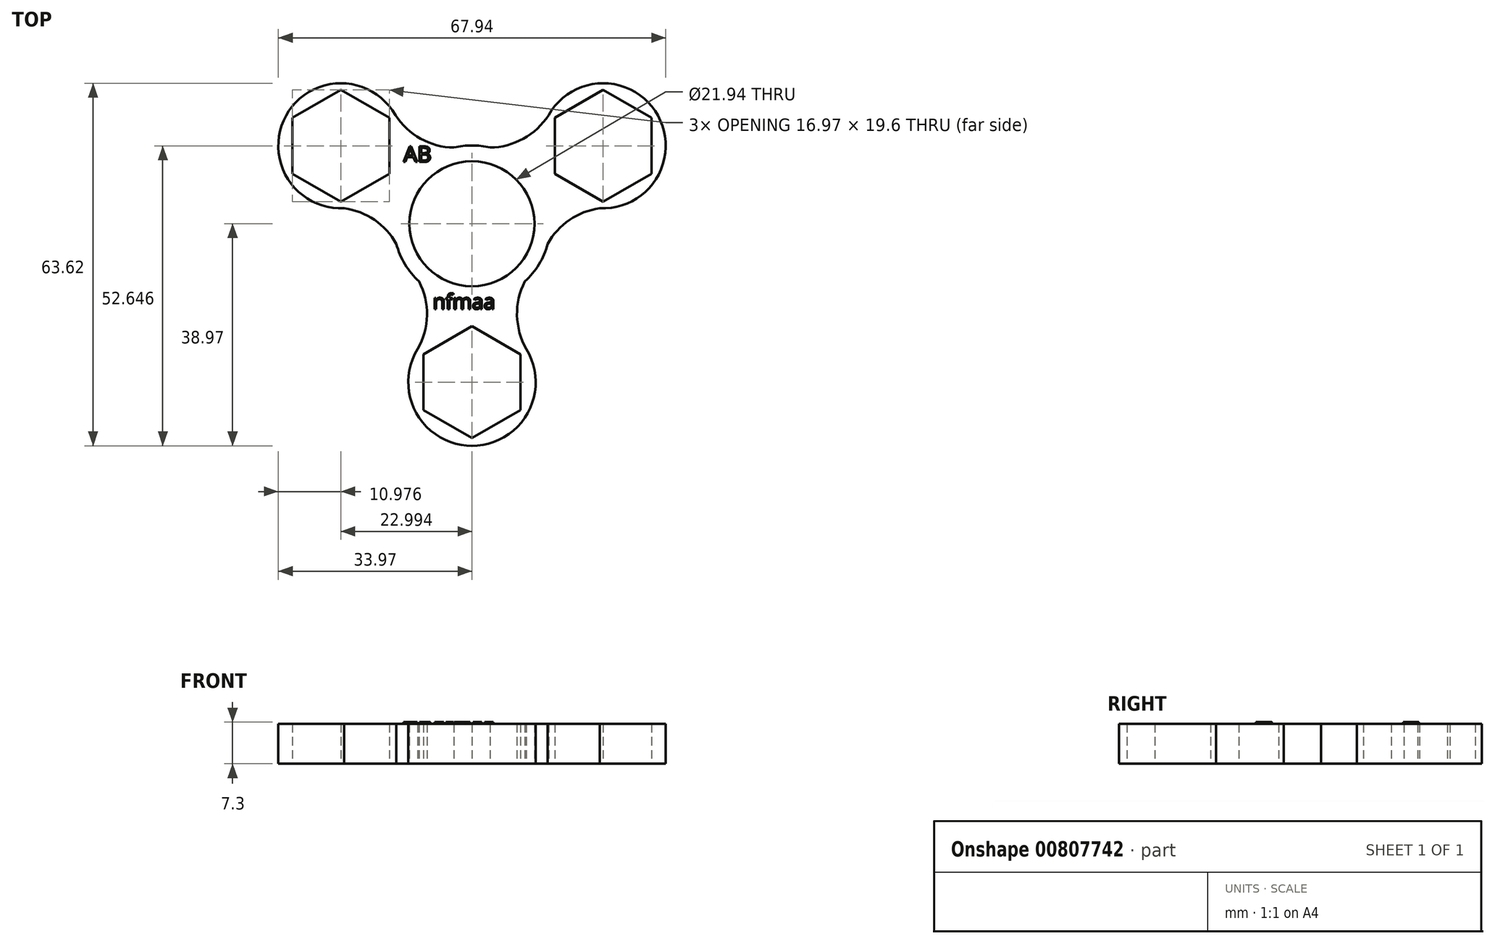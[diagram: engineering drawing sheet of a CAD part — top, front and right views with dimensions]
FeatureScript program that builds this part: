
annotation { "Feature Type Name" : "Feature", "Feature Type Description" : "" }
export const myFeature = defineFeature(function(context is Context, id is Id, definition is map)
    precondition{}
    {
        {
            var Q0;
            Q0=qCreatedBy(makeId("Top.planeOp"),FACE);
            var sketch = newSketch(context, id + "F0", { "sketchPlane" : qUnion([Q0])});
            skCircle(sketch, "E0", {"center": v(0, 0) * mm, "radius": 10.97 * mm});
            skCircle(sketch, "E1", {"center": v(0, 0) * mm, "radius": 13.74 * mm});
            skCircle(sketch, "E2", {"center": v(-23, 13.68) * mm, "radius": 10.97 * mm});
            skCircle(sketch, "E3", {"center": v(23, 13.68) * mm, "radius": 10.97 * mm});
            skCircle(sketch, "E4", {"center": v(0, -27.8) * mm, "radius": 11.17 * mm});
            skArc(sketch, "E5", {"start": v(-13.43, 19.06) * mm, "mid": v(-7.57, 14.24) * mm, "end": v(0, 13.74) * mm});
            skArc(sketch, "E6.MirrorCS", {"start": v(13.43, 19.06) * mm, "mid": v(7.57, 14.24) * mm, "end": v(0, 13.74) * mm});
            skPoint(sketch, "E7", {"position": v(-12.09, -6.52) * mm});
            skPoint(sketch, "E8", {"position": v(12.31, -6.09) * mm});
            skArc(sketch, "E9", {"start": v(-12.09, -6.52) * mm, "mid": v(-16.7, 0.37) * mm, "end": v(-24.62, 2.83) * mm});
            skArc(sketch, "E10.MirrorCS", {"start": v(12.09, -6.52) * mm, "mid": v(16.7, 0.37) * mm, "end": v(24.62, 2.83) * mm});
            skArc(sketch, "E11", {"start": v(12.09, -6.52) * mm, "mid": v(8.04, -13.96) * mm, "end": v(9.7, -22.27) * mm});
            skArc(sketch, "E12.MirrorCS", {"start": v(-12.09, -6.52) * mm, "mid": v(-8.04, -13.96) * mm, "end": v(-9.7, -22.27) * mm});
            skLineSegment(sketch, "E13.0", {"start": v(-14.5, 18.58) * mm, "end": v(-14.5, 8.78) * mm});
            skLineSegment(sketch, "E13.1", {"start": v(-14.5, 8.78) * mm, "end": v(-23, 3.88) * mm});
            skLineSegment(sketch, "E13.2", {"start": v(-23, 3.88) * mm, "end": v(-31.48, 8.78) * mm});
            skLineSegment(sketch, "E13.3", {"start": v(-31.48, 8.78) * mm, "end": v(-31.48, 18.58) * mm});
            skLineSegment(sketch, "E13.4", {"start": v(-31.48, 18.58) * mm, "end": v(-23, 23.47) * mm});
            skLineSegment(sketch, "E13.5", {"start": v(-23, 23.47) * mm, "end": v(-14.5, 18.58) * mm});
            skLineSegment(sketch, "E14.0", {"start": v(8.49, -22.9) * mm, "end": v(8.49, -32.7) * mm});
            skLineSegment(sketch, "E14.1", {"start": v(8.49, -32.7) * mm, "end": v(0, -37.6) * mm});
            skLineSegment(sketch, "E14.2", {"start": v(0, -37.6) * mm, "end": v(-8.49, -32.7) * mm});
            skLineSegment(sketch, "E14.3", {"start": v(-8.49, -32.7) * mm, "end": v(-8.49, -22.9) * mm});
            skLineSegment(sketch, "E14.4", {"start": v(-8.49, -22.9) * mm, "end": v(0, -18) * mm});
            skLineSegment(sketch, "E14.5", {"start": v(0, -18) * mm, "end": v(8.49, -22.9) * mm});
            skLineSegment(sketch, "E15.0", {"start": v(31.48, 18.58) * mm, "end": v(31.48, 8.78) * mm});
            skLineSegment(sketch, "E15.1", {"start": v(31.48, 8.78) * mm, "end": v(23, 3.88) * mm});
            skLineSegment(sketch, "E15.2", {"start": v(23, 3.88) * mm, "end": v(14.5, 8.78) * mm});
            skLineSegment(sketch, "E15.3", {"start": v(14.5, 8.78) * mm, "end": v(14.5, 18.58) * mm});
            skLineSegment(sketch, "E15.4", {"start": v(14.5, 18.58) * mm, "end": v(23, 23.47) * mm});
            skLineSegment(sketch, "E15.5", {"start": v(23, 23.47) * mm, "end": v(31.48, 18.58) * mm});
            skSolve(sketch);
        }
        {
            var Q0;
            Q0=qSketchRegion(id+"F0",true);
            extrude(context, id + "F1", {"entities" : qUnion([Q0]), "depth" : 7 * mm, "offsetDistance" : 25 * mm});
        }
        {
            var Q0;
            Q0=qCreatedBy(makeId("Top.planeOp"),FACE);
            var sketch = newSketch(context, id + "F2", { "sketchPlane" : qUnion([Q0])});
            skText(sketch, "E16", { "text": "nfmaa", "fontName": "OpenSans-Regular.ttf"});
            skText(sketch, "E17", { "text": "AB", "fontName": "OpenSans-Regular.ttf"});
            const initialGuessF2  = {"E16": [-0.00689, -0.01497, 1, 0, 0.00263], "E17": [-0.01203, 0.01084, 1, 0, 0.00276]};
            skSetInitialGuess(sketch, initialGuessF2);
            skSolve(sketch);
        }
        {
            var Q0;
            Q0=qSketchRegion(id+"F2",true);
            extrude(context, id + "F3", {"entities" : qUnion([Q0]), "operationType" : NewBodyOperationType.ADD, "depth" : 7.3 * mm, "offsetDistance" : 25 * mm});
        }
    });
